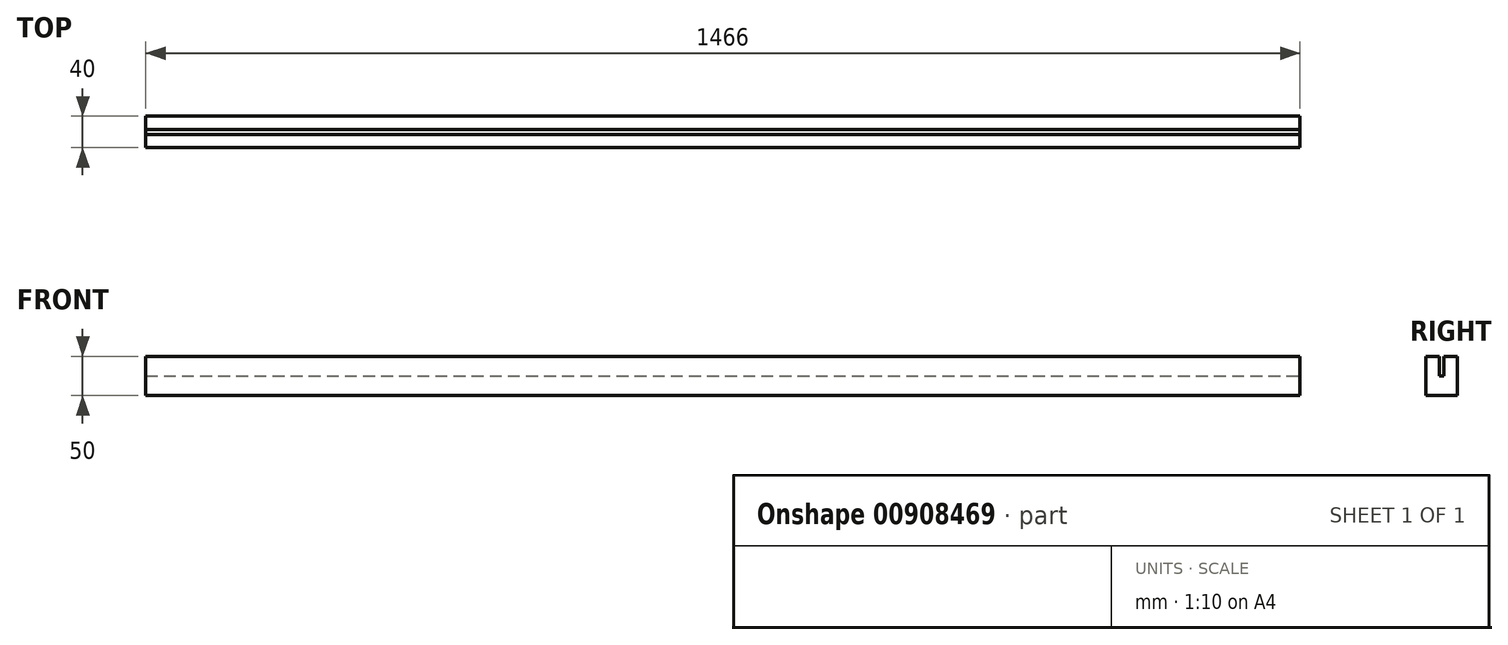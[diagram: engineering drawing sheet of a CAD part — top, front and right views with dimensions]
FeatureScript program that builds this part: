
annotation { "Feature Type Name" : "Feature", "Feature Type Description" : "" }
export const myFeature = defineFeature(function(context is Context, id is Id, definition is map)
    precondition{}
    {
        {
            var Q0;
            Q0=qCreatedBy(makeId("Top.planeOp"),FACE);
            var sketch = newSketch(context, id + "F0", { "sketchPlane" : qUnion([Q0])});
            skLineSegment(sketch, "E0.bottom", {"start": v(0, 0) * mm, "end": v(1466, 0) * mm});
            skLineSegment(sketch, "E0.top", {"start": v(0, -40) * mm, "end": v(1466, -40) * mm});
            skLineSegment(sketch, "E0.left", {"start": v(0, 0) * mm, "end": v(0, -40) * mm});
            skLineSegment(sketch, "E0.right", {"start": v(1466, 0) * mm, "end": v(1466, -40) * mm});
            skSolve(sketch);
        }
        {
            var Q0;
            Q0 = qSketchRegion(id + "F0", true);
            extrude(context, id + "F1", {"entities" : qUnion([Q0]), "depth" : 50 * mm, "offsetDistance" : 25 * mm});
        }
        {
            var Q0;
            Q0=makeQuery(id+"F1.opExtrude","CAP_FACE",FACE,{"disambiguationData":[OSD([sQuery(id+"F0.wireOp",EDGE,"E0.bottom"),sQuery(id+"F0.wireOp",EDGE,"E0.top"),sQuery(id+"F0.wireOp",EDGE,"E0.left"),sQuery(id+"F0.wireOp",EDGE,"E0.right")])],"isStart":false});
            var sketch = newSketch(context, id + "F2", { "sketchPlane" : qUnion([Q0])});
            skLineSegment(sketch, "E1", {"start": v(0, -20) * mm, "end": v(1466, -20) * mm, "construction": true});
            skLineSegment(sketch, "E2", {"start": v(0, -20) * mm, "end": v(0, -23) * mm});
            skLineSegment(sketch, "E3", {"start": v(0, -17) * mm, "end": v(1466, -17) * mm});
            skLineSegment(sketch, "E4", {"start": v(1466, -17) * mm, "end": v(1466, -20) * mm});
            skLineSegment(sketch, "E5", {"start": v(1466, -20) * mm, "end": v(1466, -23) * mm});
            skLineSegment(sketch, "E6", {"start": v(1466, -23) * mm, "end": v(0, -23) * mm});
            skLineSegment(sketch, "E7", {"start": v(0, -17) * mm, "end": v(0, -20) * mm});
            skSolve(sketch);
        }
        {
            var Q0;
            Q0 = qSketchRegion(id + "F2", true);
            extrude(context, id + "F3", {"entities" : qUnion([Q0]), "operationType" : NewBodyOperationType.REMOVE, "oppositeDirection" : true, "depth" : 25 * mm, "offsetDistance" : 25 * mm});
        }
    });
